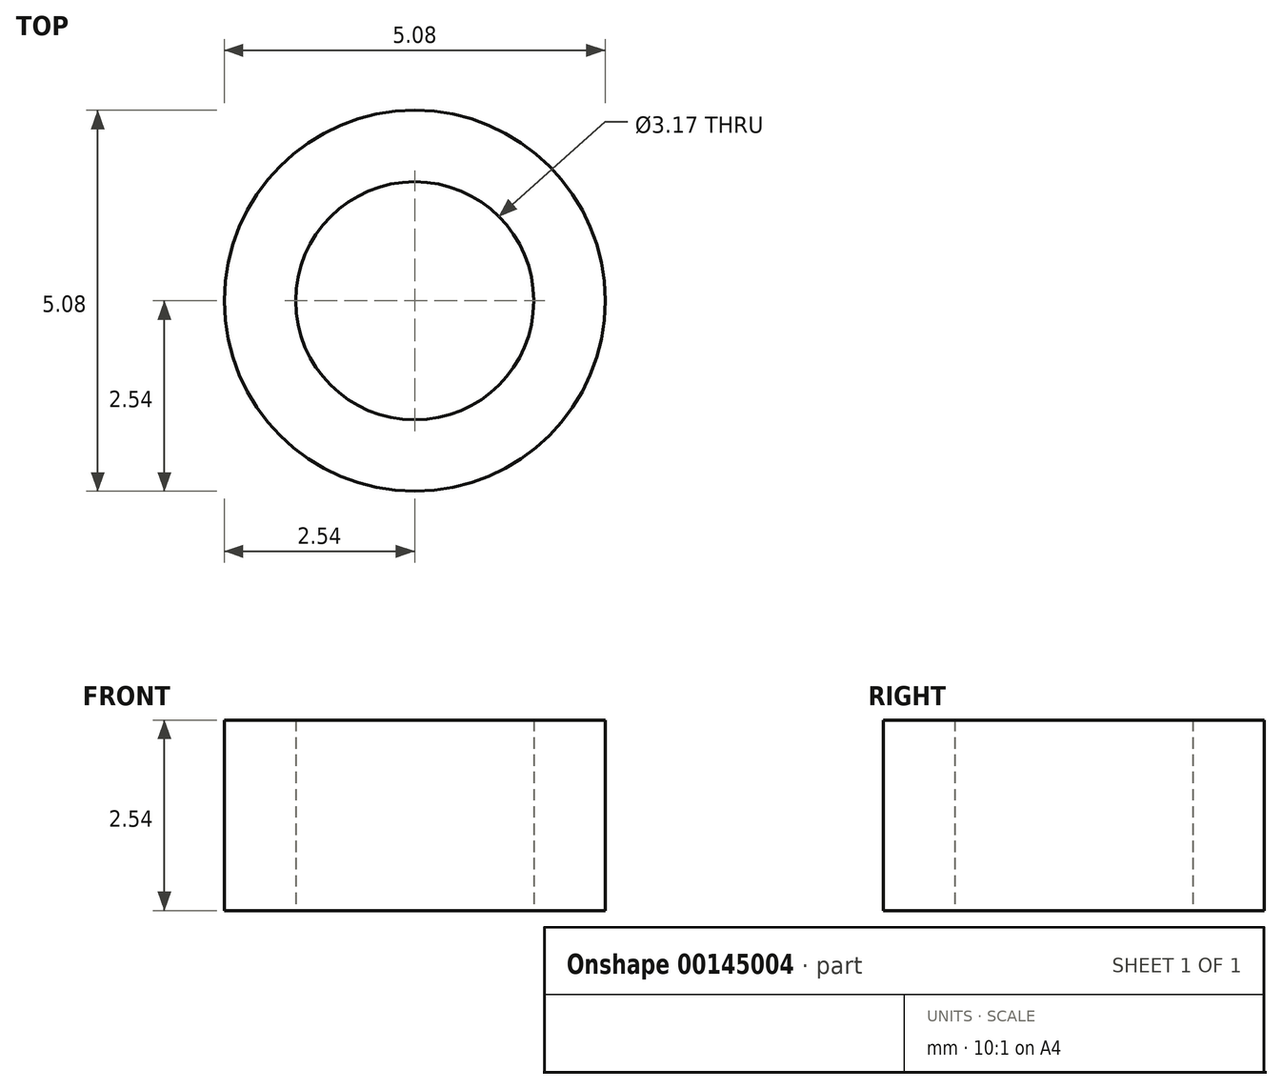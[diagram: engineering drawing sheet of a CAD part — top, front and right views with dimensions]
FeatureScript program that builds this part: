
annotation { "Feature Type Name" : "Feature", "Feature Type Description" : "" }
export const myFeature = defineFeature(function(context is Context, id is Id, definition is map)
    precondition{}
    {
        {
            var Q0;
            Q0=qCreatedBy(makeId("Top.planeOp"),FACE);
            var sketch = newSketch(context, id + "F0", { "sketchPlane" : qUnion([Q0])});
            skCircle(sketch, "E0", {"center": v(0, 0) * mm, "radius": 1.59 * mm});
            skCircle(sketch, "E1", {"center": v(0, 0) * mm, "radius": 2.54 * mm});
            skSolve(sketch);
        }
        {
            var Q0;
            Q0 = qSketchRegion(id + "F0", true);
            extrude(context, id + "F1", {"entities" : qUnion([Q0]), "depth" : 2.54 * mm});
        }
    });
